# Revit family: JAF-VI_Eng
name_source: partatom
category: Оборудование
units: mm (PartAtom-declared; Revit-internal decimal feet)

## family parameters
Всегда вертикально = Да
Классификация = Нет
На основе рабочей плоскости = Нет
Общий = Нет
При загрузке вырезать с полостями = Нет
Размер круглого соединителя = Использовать диаметр
Тип детали = Нормальный
Точка принадлежности помещению = Нет

## types (54) — shared parameters
00_20_Manufacturer = Vents
00_20_Name = Impulse axial fan
Casing Material = Metal, painted, blue, matte RAL 5007
Frequency = 50 Гц
Load Classification = HVAC
Maintenance zone material = <По категории>
Number of phases = 3
Thrust = 0.00 Н
URL = https://ventilation-system.com
Voltage = 400 В
Изготовитель = Vents
zero-valued in all types: Отметка по умолчанию

## per-type parameters (varying)
| type | A | B | D | H | Height | L | L1 | L2 | Length | Motor | Power | R | Trellis | Weight | Width | h | h1 | h2 | l1 | lattice |
| JAF-VI-315-2-U-300/2 | 700 мм | 542 мм | 315 мм | 347 мм | 347 мм | 1846 мм | 507 мм | 572 мм | 1846 мм | Motor : Motor_315 | 550 Вт | Нет | Trellis : 315 | 58.00 кг | 572 мм | 174 мм | 86 мм | 58 мм | 254 мм | Да |
| JAF-VI-400-2/4-R-300/2 | 750 мм | 632 мм | 400 мм | 434 мм | 434 мм | 2296 мм | 590 мм | 667 мм | 2296 мм | Motor : Motor_400 | 1500 Вт | Да | Trellis : 400 | 95.00 кг | 667 мм | 217 мм | 108 мм | 72 мм | 295 мм | Нет |
| JAF-VI-355M-2-U | 700 мм | 583 мм | 355 мм | 388 мм | 388 мм | 2046 мм | 546 мм | 613 мм | 2046 мм | Motor : Motor_355 | 1100 Вт | Нет | Trellis : 355 | 75.00 кг | 613 мм | 194 мм | 96 мм | 65 мм | 273 мм | Да |
| JAF-VI-315-2/4-R-400/2 | 700 мм | 542 мм | 315 мм | 347 мм | 347 мм | 1846 мм | 507 мм | 572 мм | 1846 мм | Motor : Motor_315 | 550 Вт | Да | Trellis : 315 | 58.00 кг | 572 мм | 174 мм | 86 мм | 58 мм | 254 мм | Нет |
| JAF-VI-355-2/4-R-300/2 | 700 мм | 583 мм | 355 мм | 388 мм | 388 мм | 2046 мм | 546 мм | 613 мм | 2046 мм | Motor : Motor_355 | 1100 Вт | Да | Trellis : 355 | 75.00 кг | 613 мм | 194 мм | 96 мм | 65 мм | 273 мм | Нет |
| JAF-VI-400-2-U-400/2 | 750 мм | 632 мм | 400 мм | 434 мм | 434 мм | 2296 мм | 590 мм | 667 мм | 2296 мм | Motor : Motor_400 | 1100 Вт | Нет | Trellis : 400 | 95.00 кг | 667 мм | 217 мм | 108 мм | 72 мм | 295 мм | Да |
| JAF-VI-315M-2/4-U | 700 мм | 542 мм | 315 мм | 347 мм | 347 мм | 1846 мм | 507 мм | 572 мм | 1846 мм | Motor : Motor_315 | 800 Вт | Нет | Trellis : 315 | 58.00 кг | 572 мм | 174 мм | 86 мм | 58 мм | 254 мм | Да |
| JAF-VI-355-2/4-U-400/2 | 700 мм | 583 мм | 355 мм | 388 мм | 388 мм | 2046 мм | 546 мм | 613 мм | 2046 мм | Motor : Motor_355 | 800 Вт | Нет | Trellis : 355 | 75.00 кг | 613 мм | 194 мм | 96 мм | 65 мм | 273 мм | Да |
| JAF-VI-400-2/4-U-300/2 | 750 мм | 632 мм | 400 мм | 434 мм | 434 мм | 2296 мм | 590 мм | 667 мм | 2296 мм | Motor : Motor_400 | 1100 Вт | Нет | Trellis : 400 | 95.00 кг | 667 мм | 217 мм | 108 мм | 72 мм | 295 мм | Да |
| JAF-VI-315-2-U | 700 мм | 542 мм | 315 мм | 347 мм | 347 мм | 1846 мм | 507 мм | 572 мм | 1846 мм | Motor : Motor_315 | 550 Вт | Нет | Trellis : 315 | 58.00 кг | 572 мм | 174 мм | 86 мм | 58 мм | 254 мм | Да |
| JAF-VI-315-2-U-400/2 | 700 мм | 542 мм | 315 мм | 347 мм | 347 мм | 1846 мм | 507 мм | 572 мм | 1846 мм | Motor : Motor_315 | 550 Вт | Нет | Trellis : 315 | 58.00 кг | 572 мм | 174 мм | 86 мм | 58 мм | 254 мм | Да |
| JAF-VI-315M-2-U | 700 мм | 542 мм | 315 мм | 347 мм | 347 мм | 1846 мм | 507 мм | 572 мм | 1846 мм | Motor : Motor_315 | 750 Вт | Нет | Trellis : 315 | 58.00 кг | 572 мм | 174 мм | 86 мм | 58 мм | 254 мм | Да |
| JAF-VI-315M-2-U-300/2 | 700 мм | 542 мм | 315 мм | 347 мм | 347 мм | 1846 мм | 507 мм | 572 мм | 1846 мм | Motor : Motor_315 | 750 Вт | Нет | Trellis : 315 | 58.00 кг | 572 мм | 174 мм | 86 мм | 58 мм | 254 мм | Да |
| JAF-VI-315M-2-U-400/2 | 700 мм | 542 мм | 315 мм | 347 мм | 347 мм | 1846 мм | 507 мм | 572 мм | 1846 мм | Motor : Motor_315 | 750 Вт | Нет | Trellis : 315 | 58.00 кг | 572 мм | 174 мм | 86 мм | 58 мм | 254 мм | Да |
| JAF-VI-315-2/4-U | 700 мм | 542 мм | 315 мм | 347 мм | 347 мм | 1846 мм | 507 мм | 572 мм | 1846 мм | Motor : Motor_315 | 550 Вт | Нет | Trellis : 315 | 58.00 кг | 572 мм | 174 мм | 86 мм | 58 мм | 254 мм | Да |
| JAF-VI-315-2/4-U-300/2 | 700 мм | 542 мм | 315 мм | 347 мм | 347 мм | 1846 мм | 507 мм | 572 мм | 1846 мм | Motor : Motor_315 | 550 Вт | Нет | Trellis : 315 | 58.00 кг | 572 мм | 174 мм | 86 мм | 58 мм | 254 мм | Да |
| JAF-VI-315-2/4-U-400/2 | 700 мм | 542 мм | 315 мм | 347 мм | 347 мм | 1846 мм | 507 мм | 572 мм | 1846 мм | Motor : Motor_315 | 550 Вт | Нет | Trellis : 315 | 58.00 кг | 572 мм | 174 мм | 86 мм | 58 мм | 254 мм | Да |
| JAF-VI-315M-2/4-U-300/2 | 700 мм | 542 мм | 315 мм | 347 мм | 347 мм | 1846 мм | 507 мм | 572 мм | 1846 мм | Motor : Motor_315 | 800 Вт | Нет | Trellis : 315 | 58.00 кг | 572 мм | 174 мм | 86 мм | 58 мм | 254 мм | Да |
| JAF-VI-315M-2/4-U-400/2 | 700 мм | 542 мм | 315 мм | 347 мм | 347 мм | 1846 мм | 507 мм | 572 мм | 1846 мм | Motor : Motor_315 | 800 Вт | Нет | Trellis : 315 | 58.00 кг | 572 мм | 174 мм | 86 мм | 58 мм | 254 мм | Да |
| JAF-VI-315-2-R | 700 мм | 542 мм | 315 мм | 347 мм | 347 мм | 1846 мм | 507 мм | 572 мм | 1846 мм | Motor : Motor_315 | 550 Вт | Да | Trellis : 315 | 58.00 кг | 572 мм | 174 мм | 86 мм | 58 мм | 254 мм | Нет |
| JAF-VI-315-2-R-300/2 | 700 мм | 542 мм | 315 мм | 347 мм | 347 мм | 1846 мм | 507 мм | 572 мм | 1846 мм | Motor : Motor_315 | 550 Вт | Да | Trellis : 315 | 58.00 кг | 572 мм | 174 мм | 86 мм | 58 мм | 254 мм | Нет |
| JAF-VI-315-2-R-400/2 | 700 мм | 542 мм | 315 мм | 347 мм | 347 мм | 1846 мм | 507 мм | 572 мм | 1846 мм | Motor : Motor_315 | 550 Вт | Да | Trellis : 315 | 58.00 кг | 572 мм | 174 мм | 86 мм | 58 мм | 254 мм | Нет |
| JAF-VI-315-2/4-R | 700 мм | 542 мм | 315 мм | 347 мм | 347 мм | 1846 мм | 507 мм | 572 мм | 1846 мм | Motor : Motor_315 | 550 Вт | Да | Trellis : 315 | 58.00 кг | 572 мм | 174 мм | 86 мм | 58 мм | 254 мм | Нет |
| JAF-VI-315-2/4-R-300/2 | 700 мм | 542 мм | 315 мм | 347 мм | 347 мм | 1846 мм | 507 мм | 572 мм | 1846 мм | Motor : Motor_315 | 550 Вт | Да | Trellis : 315 | 58.00 кг | 572 мм | 174 мм | 86 мм | 58 мм | 254 мм | Нет |
| JAF-VI-355-2/4-R | 700 мм | 583 мм | 355 мм | 388 мм | 388 мм | 2046 мм | 546 мм | 613 мм | 2046 мм | Motor : Motor_355 | 1100 Вт | Да | Trellis : 355 | 75.00 кг | 613 мм | 194 мм | 96 мм | 65 мм | 273 мм | Нет |
| JAF-VI-355-2-R-300/2 | 700 мм | 583 мм | 355 мм | 388 мм | 388 мм | 2046 мм | 546 мм | 613 мм | 2046 мм | Motor : Motor_355 | 1100 Вт | Да | Trellis : 355 | 75.00 кг | 613 мм | 194 мм | 96 мм | 65 мм | 273 мм | Нет |
| JAF-VI-355-2-R | 700 мм | 583 мм | 355 мм | 388 мм | 388 мм | 2046 мм | 546 мм | 613 мм | 2046 мм | Motor : Motor_355 | 1100 Вт | Да | Trellis : 355 | 75.00 кг | 613 мм | 194 мм | 96 мм | 65 мм | 273 мм | Нет |
| JAF-VI-355-2-R-400/2 | 700 мм | 583 мм | 355 мм | 388 мм | 388 мм | 2046 мм | 546 мм | 613 мм | 2046 мм | Motor : Motor_355 | 1100 Вт | Да | Trellis : 355 | 75.00 кг | 613 мм | 194 мм | 96 мм | 65 мм | 273 мм | Нет |
| JAF-VI-355-2/4-R-400/2 | 700 мм | 583 мм | 355 мм | 388 мм | 388 мм | 2046 мм | 546 мм | 613 мм | 2046 мм | Motor : Motor_355 | 1100 Вт | Да | Trellis : 355 | 75.00 кг | 613 мм | 194 мм | 96 мм | 65 мм | 273 мм | Нет |
| JAF-VI-355-2-U | 700 мм | 583 мм | 355 мм | 388 мм | 388 мм | 2046 мм | 546 мм | 613 мм | 2046 мм | Motor : Motor_355 | 750 Вт | Нет | Trellis : 355 | 75.00 кг | 613 мм | 194 мм | 96 мм | 65 мм | 273 мм | Да |
| JAF-VI-355-2-U-300/2 | 700 мм | 583 мм | 355 мм | 388 мм | 388 мм | 2046 мм | 546 мм | 613 мм | 2046 мм | Motor : Motor_355 | 750 Вт | Нет | Trellis : 355 | 75.00 кг | 613 мм | 194 мм | 96 мм | 65 мм | 273 мм | Да |
| JAF-VI-355-2-U-400/2 | 700 мм | 583 мм | 355 мм | 388 мм | 388 мм | 2046 мм | 546 мм | 613 мм | 2046 мм | Motor : Motor_355 | 750 Вт | Нет | Trellis : 355 | 75.00 кг | 613 мм | 194 мм | 96 мм | 65 мм | 273 мм | Да |
| JAF-VI-355M-2-U-300/2 | 700 мм | 583 мм | 355 мм | 388 мм | 388 мм | 2046 мм | 546 мм | 613 мм | 2046 мм | Motor : Motor_355 | 1100 Вт | Нет | Trellis : 355 | 75.00 кг | 613 мм | 194 мм | 96 мм | 65 мм | 273 мм | Да |
| JAF-VI-355M-2-U-400/2 | 700 мм | 583 мм | 355 мм | 388 мм | 388 мм | 2046 мм | 546 мм | 613 мм | 2046 мм | Motor : Motor_355 | 1100 Вт | Нет | Trellis : 355 | 75.00 кг | 613 мм | 194 мм | 96 мм | 65 мм | 273 мм | Да |
| JAF-VI-355-2/4-U | 700 мм | 583 мм | 355 мм | 388 мм | 388 мм | 2046 мм | 546 мм | 613 мм | 2046 мм | Motor : Motor_355 | 800 Вт | Нет | Trellis : 355 | 75.00 кг | 613 мм | 194 мм | 96 мм | 65 мм | 273 мм | Да |
| JAF-VI-355-2/4-U-300/2 | 700 мм | 583 мм | 355 мм | 388 мм | 388 мм | 2046 мм | 546 мм | 613 мм | 2046 мм | Motor : Motor_355 | 800 Вт | Нет | Trellis : 355 | 75.00 кг | 613 мм | 194 мм | 96 мм | 65 мм | 273 мм | Да |
| JAF-VI-355M-2/4-U | 700 мм | 583 мм | 355 мм | 388 мм | 388 мм | 2046 мм | 546 мм | 613 мм | 2046 мм | Motor : Motor_355 | 1100 Вт | Нет | Trellis : 355 | 75.00 кг | 613 мм | 194 мм | 96 мм | 65 мм | 273 мм | Да |
| JAF-VI-355M-2/4-U-300/2 | 700 мм | 583 мм | 355 мм | 388 мм | 388 мм | 2046 мм | 546 мм | 613 мм | 2046 мм | Motor : Motor_355 | 1100 Вт | Нет | Trellis : 355 | 75.00 кг | 613 мм | 194 мм | 96 мм | 65 мм | 273 мм | Да |
| JAF-VI-355M-2/4-U-400/2 | 700 мм | 583 мм | 355 мм | 388 мм | 388 мм | 2046 мм | 546 мм | 613 мм | 2046 мм | Motor : Motor_355 | 1100 Вт | Нет | Trellis : 355 | 75.00 кг | 613 мм | 194 мм | 96 мм | 65 мм | 273 мм | Да |
| JAF-VI-400-2/4-R | 750 мм | 632 мм | 400 мм | 434 мм | 434 мм | 2296 мм | 590 мм | 667 мм | 2296 мм | Motor : Motor_400 | 1500 Вт | Да | Trellis : 400 | 95.00 кг | 667 мм | 217 мм | 108 мм | 72 мм | 295 мм | Нет |
| JAF-VI-400-2-R | 750 мм | 632 мм | 400 мм | 434 мм | 434 мм | 2296 мм | 590 мм | 667 мм | 2296 мм | Motor : Motor_400 | 1500 Вт | Да | Trellis : 400 | 95.00 кг | 667 мм | 217 мм | 108 мм | 72 мм | 295 мм | Нет |
| JAF-VI-400-2-R-300/2 | 750 мм | 632 мм | 400 мм | 434 мм | 434 мм | 2296 мм | 590 мм | 667 мм | 2296 мм | Motor : Motor_400 | 1500 Вт | Да | Trellis : 400 | 95.00 кг | 667 мм | 217 мм | 108 мм | 72 мм | 295 мм | Нет |
| JAF-VI-400-2-R-400/2 | 750 мм | 632 мм | 400 мм | 434 мм | 434 мм | 2296 мм | 590 мм | 667 мм | 2296 мм | Motor : Motor_400 | 1500 Вт | Да | Trellis : 400 | 95.00 кг | 667 мм | 217 мм | 108 мм | 72 мм | 295 мм | Нет |
| JAF-VI-400-2/4-R-400/2 | 750 мм | 632 мм | 400 мм | 434 мм | 434 мм | 2296 мм | 590 мм | 667 мм | 2296 мм | Motor : Motor_400 | 1500 Вт | Да | Trellis : 400 | 95.00 кг | 667 мм | 217 мм | 108 мм | 72 мм | 295 мм | Нет |
| JAF-VI-400-2-U | 750 мм | 632 мм | 400 мм | 434 мм | 434 мм | 2296 мм | 590 мм | 667 мм | 2296 мм | Motor : Motor_400 | 1100 Вт | Нет | Trellis : 400 | 95.00 кг | 667 мм | 217 мм | 108 мм | 72 мм | 295 мм | Да |
| JAF-VI-400-2-U-300/2 | 750 мм | 632 мм | 400 мм | 434 мм | 434 мм | 2296 мм | 590 мм | 667 мм | 2296 мм | Motor : Motor_400 | 1100 Вт | Нет | Trellis : 400 | 95.00 кг | 667 мм | 217 мм | 108 мм | 72 мм | 295 мм | Да |
| JAF-VI-400M-2-U-400/2 | 750 мм | 632 мм | 400 мм | 434 мм | 434 мм | 2296 мм | 590 мм | 667 мм | 2296 мм | Motor : Motor_400 | 2200 Вт | Нет | Trellis : 400 | 95.00 кг | 667 мм | 217 мм | 108 мм | 72 мм | 295 мм | Да |
| JAF-VI-400-2/4-U | 750 мм | 632 мм | 400 мм | 434 мм | 434 мм | 2296 мм | 590 мм | 667 мм | 2296 мм | Motor : Motor_400 | 1100 Вт | Нет | Trellis : 400 | 95.00 кг | 667 мм | 217 мм | 108 мм | 72 мм | 295 мм | Да |
| JAF-VI-400M-2/4-U-400/2 | 750 мм | 632 мм | 400 мм | 434 мм | 434 мм | 2296 мм | 590 мм | 667 мм | 2296 мм | Motor : Motor_400 | 2200 Вт | Нет | Trellis : 400 | 95.00 кг | 667 мм | 217 мм | 108 мм | 72 мм | 295 мм | Да |
| JAF-VI-400-2/4-U-400/2 | 750 мм | 632 мм | 400 мм | 434 мм | 434 мм | 2296 мм | 590 мм | 667 мм | 2296 мм | Motor : Motor_400 | 1100 Вт | Нет | Trellis : 400 | 95.00 кг | 667 мм | 217 мм | 108 мм | 72 мм | 295 мм | Да |
| JAF-VI-400M-2-U | 750 мм | 632 мм | 400 мм | 434 мм | 434 мм | 2296 мм | 590 мм | 667 мм | 2296 мм | Motor : Motor_400 | 2200 Вт | Нет | Trellis : 400 | 95.00 кг | 667 мм | 217 мм | 108 мм | 72 мм | 295 мм | Да |
| JAF-VI-400M-2-U-300/2 | 750 мм | 632 мм | 400 мм | 434 мм | 434 мм | 2296 мм | 590 мм | 667 мм | 2296 мм | Motor : Motor_400 | 2200 Вт | Нет | Trellis : 400 | 95.00 кг | 667 мм | 217 мм | 108 мм | 72 мм | 295 мм | Да |
| JAF-VI-400M-2/4-U | 750 мм | 632 мм | 400 мм | 434 мм | 434 мм | 2296 мм | 590 мм | 667 мм | 2296 мм | Motor : Motor_400 | 2200 Вт | Нет | Trellis : 400 | 95.00 кг | 667 мм | 217 мм | 108 мм | 72 мм | 295 мм | Да |
| JAF-VI-400M-2/4-U-300/2 | 750 мм | 632 мм | 400 мм | 434 мм | 434 мм | 2296 мм | 590 мм | 667 мм | 2296 мм | Motor : Motor_400 | 2200 Вт | Нет | Trellis : 400 | 95.00 кг | 667 мм | 217 мм | 108 мм | 72 мм | 295 мм | Да |

note: column(s) folded — value = type name in every type: 00_20_Type
